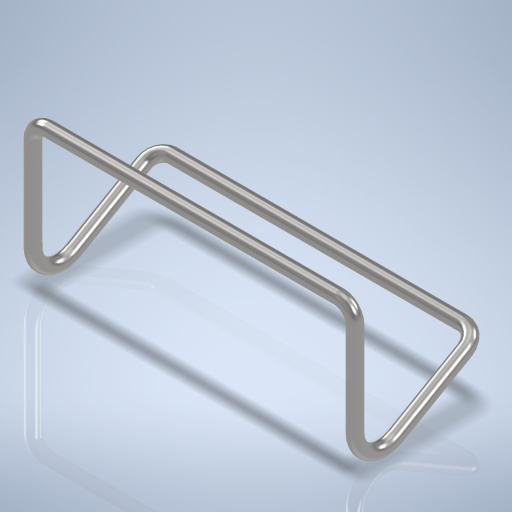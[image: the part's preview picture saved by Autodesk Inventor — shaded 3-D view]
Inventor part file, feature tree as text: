
AUTODESK INVENTOR PART (.ipt)
format: ipt  version: 2024 (Build 280153000, 153)  size: 371,200 bytes
history: native  units: mm
features: sketch x8, plane x7, other x7, sweep x4, mirror x1, projected_geometry x1
ambient origin geometry x8: Origin, YZ Plane, XZ Plane, XY Plane, X Axis, Y Axis, Z Axis, Center Point
bodies: Volumenkörper1 (feature_tree)
feature tree (28):
  sketch  "Skizze1"  dims[d0=10.0mm d1=0.0mm]
  plane  "Arbeitsebene1"
  sweep  "Sweeping1"
  sweep  "Sweeping2"
  other  "Arbeitsachse1"
  plane  "Arbeitsebene11"
  sketch  "Skizze25"  dims[d17=12.0mm]
  plane  "Arbeitsebene12"
  sweep  "Sweeping4"
  plane  "Arbeitsebene15"
  sketch  "Skizze27"  dims[d40=180.0mm]
  plane  "Arbeitsebene16"
  plane  "Arbeitsebene18"
  mirror  "Spiegeln2"
  sweep  "Sweeping5"
  other  "Arbeitsachse4"
  other  "Arbeitsachse5"
  other  "Arbeitsachse6"
  plane  "Arbeitsebene17"
  sketch  "Skizze2"  dims[d4=0.0mm d5=0.0mm d6=70.0mm]
  sketch  "Skizze8"  dims[d11=60.0deg d12=60.0mm]
  projected_geometry  "Projizierte Kontur3"
  sketch  "Skizze9"  dims[d13=20.0mm d16=180.0mm]
  other  "Arbeitsachse2"
  other  "Arbeitspunkt1"
  other  "Arbeitsachse3"
  sketch  "Skizze26"  dims[d18=0.0mm d19=0.0mm]
  sketch  "Skizze28"  dims[d41=12.0mm d42=-192.0mm d43=10.0mm d44=0.0mm d45=0.0mm d48=0.0mm d49=12.0mm d50=-70.25mm d51=10.0mm d52=0.0mm d53=0.0mm d54=-102.0mm d55=-120.0mm]
